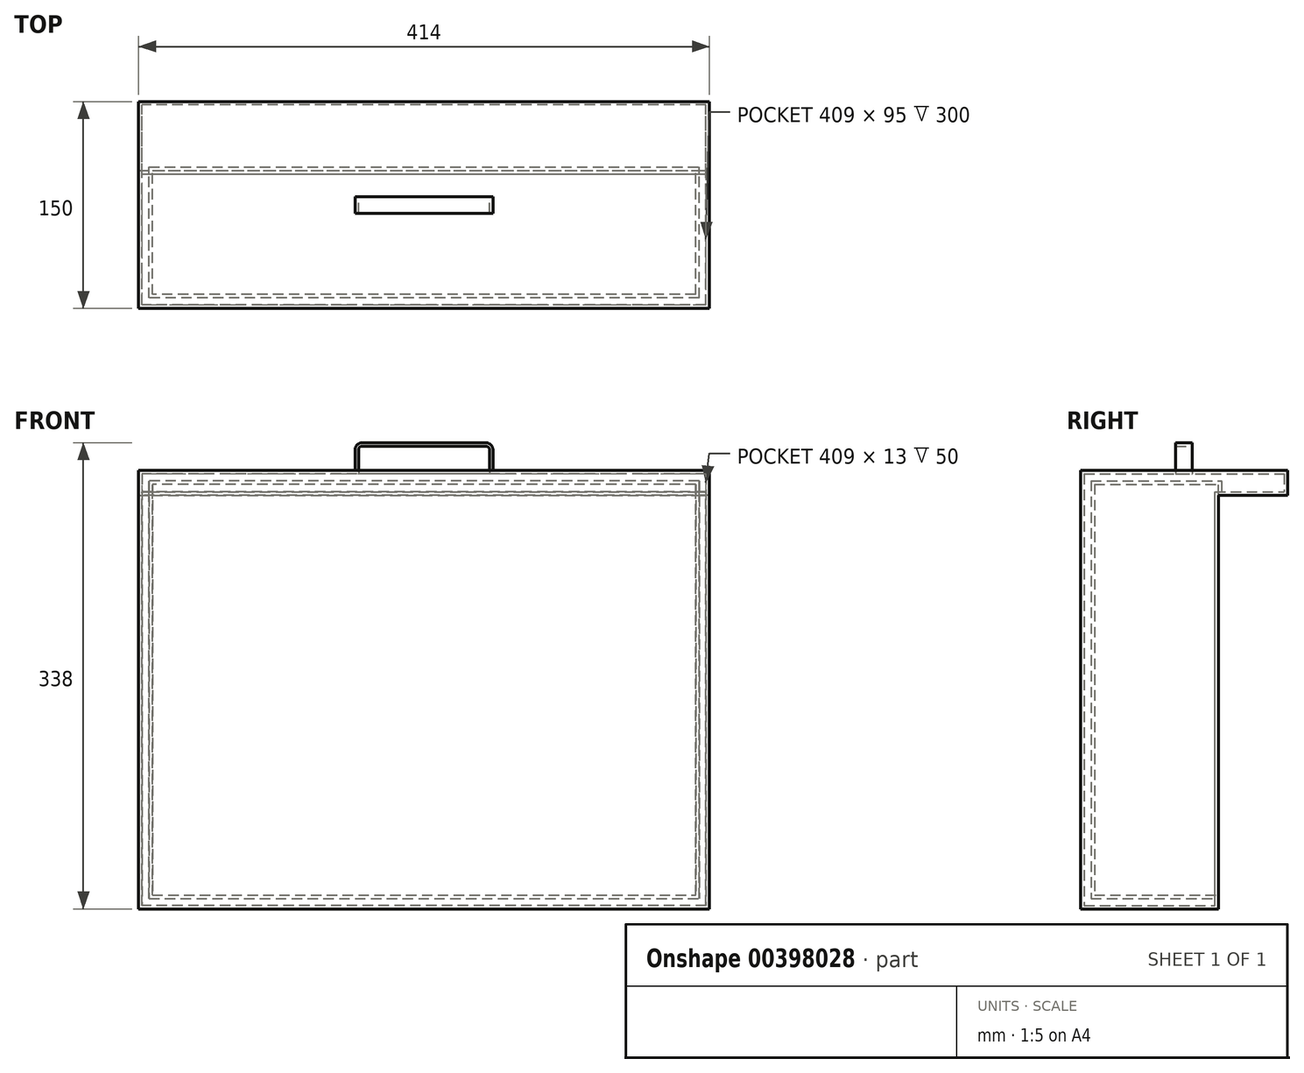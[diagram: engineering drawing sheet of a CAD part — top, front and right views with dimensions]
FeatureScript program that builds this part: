
annotation { "Feature Type Name" : "Feature", "Feature Type Description" : "" }
export const myFeature = defineFeature(function(context is Context, id is Id, definition is map)
    precondition{}
    {
        {
            var Q0;
            Q0=qCreatedBy(makeId("Top.planeOp"),FACE);
            var sketch = newSketch(context, id + "F0", { "sketchPlane" : qUnion([Q0])});
            skLineSegment(sketch, "E0.bottom", {"start": v(207, -75) * mm, "end": v(-207, -75) * mm});
            skLineSegment(sketch, "E0.top", {"start": v(207, 75) * mm, "end": v(-207, 75) * mm});
            skLineSegment(sketch, "E0.left", {"start": v(207, -75) * mm, "end": v(207, 75) * mm});
            skLineSegment(sketch, "E0.right", {"start": v(-207, -75) * mm, "end": v(-207, 75) * mm});
            skPoint(sketch, "E0.middle", {"position": v(0, 0) * mm});
            skSolve(sketch);
        }
        {
            var Q0;
            Q0 = qSketchRegion(id + "F0", true);
            extrude(context, id + "F1", {"entities" : qUnion([Q0]), "depth" : 18 * mm});
        }
        {
            var Q0;
            Q0=makeQuery(id+"F1.opExtrude","CAP_FACE",FACE,{"disambiguationData":[OSD([sQuery(id+"F0.wireOp",EDGE,"E0.bottom"),sQuery(id+"F0.wireOp",EDGE,"E0.top"),sQuery(id+"F0.wireOp",EDGE,"E0.left"),sQuery(id+"F0.wireOp",EDGE,"E0.right")])],"isStart":true});
            var sketch = newSketch(context, id + "F2", { "sketchPlane" : qUnion([Q0])});
            skLineSegment(sketch, "E1.bottom", {"start": v(-207, 75) * mm, "end": v(207, 75) * mm});
            skLineSegment(sketch, "E1.top", {"start": v(-207, -25) * mm, "end": v(207, -25) * mm});
            skLineSegment(sketch, "E1.left", {"start": v(-207, 75) * mm, "end": v(-207, -25) * mm});
            skLineSegment(sketch, "E1.right", {"start": v(207, 75) * mm, "end": v(207, -25) * mm});
            skSolve(sketch);
        }
        {
            var Q0;
            Q0 = qSketchRegion(id + "F2", true);
            extrude(context, id + "F3", {"entities" : qUnion([Q0]), "operationType" : NewBodyOperationType.ADD, "depth" : 300 * mm});
        }
        {
            var Q0;
            Q0=makeQuery(id+"F3.opExtrude","SWEPT_FACE",FACE,{"disambiguationData":[OSD([sQuery(id+"F2.wireOp",EDGE,"E1.top")])]});
            shell(context, id + "F4", {"entities" : qUnion([Q0]), "thickness" : 10 * mm});
        }
        {
            var Q0;
            Q0=makeQuery(id+"F1.opExtrude","CAP_FACE",FACE,{"disambiguationData":[OSD([sQuery(id+"F0.wireOp",EDGE,"E0.bottom"),sQuery(id+"F0.wireOp",EDGE,"E0.top"),sQuery(id+"F0.wireOp",EDGE,"E0.left"),sQuery(id+"F0.wireOp",EDGE,"E0.right")])],"isStart":false});
            var sketch = newSketch(context, id + "F5", { "sketchPlane" : qUnion([Q0])});
            skLineSegment(sketch, "E2.bottom", {"start": v(50, -6) * mm, "end": v(-50, -6) * mm});
            skLineSegment(sketch, "E2.top", {"start": v(50, 6) * mm, "end": v(-50, 6) * mm});
            skLineSegment(sketch, "E2.left", {"start": v(50, -6) * mm, "end": v(50, 6) * mm});
            skLineSegment(sketch, "E2.right", {"start": v(-50, -6) * mm, "end": v(-50, 6) * mm});
            skPoint(sketch, "E2.middle", {"position": v(0, 0) * mm});
            skSolve(sketch);
        }
        {
            var Q0;
            Q0=makeQuery(id+"F5.imprint","IMPRINT",FACE,{"disambiguationData":[TD([[makeQuery(id+"F5.imprint","IMPRINT",EDGE,{"derivedFrom":sQuery(id+"F5.wireOp",EDGE,"E2.bottom")}),-1.0]])]});
            extrude(context, id + "F6", {"entities" : qUnion([Q0]), "operationType" : NewBodyOperationType.ADD, "depth" : 20 * mm});
        }
        {
            var Q0;
            Q0=makeQuery(id+"F6.opExtrude","CAP_EDGE",EDGE,{"disambiguationData":[OSD([sQuery(id+"F5.wireOp",EDGE,"E2.left")])],"isStart":false});
            var Q1;
            Q1=makeQuery(id+"F6.opExtrude","CAP_EDGE",EDGE,{"disambiguationData":[OSD([sQuery(id+"F5.wireOp",EDGE,"E2.right")])],"isStart":false});
            fillet(context, id + "F7", {"entities" : qUnion([Q0, Q1]), "radius" : 5 * mm, "tangentPropagation" : true, "allowEdgeOverflow" : false});
        }
        {
            var Q0;
            Q0=makeQuery(id+"F6.opExtrude","SWEPT_FACE",FACE,{"disambiguationData":[OSD([sQuery(id+"F5.wireOp",EDGE,"E2.bottom")])]});
            var Q1;
            Q1=makeQuery(id+"F6.opExtrude","SWEPT_FACE",FACE,{"disambiguationData":[OSD([sQuery(id+"F5.wireOp",EDGE,"E2.top")])]});
            var Q2;
            Q2=makeQuery(id+"F1.opExtrude","SWEPT_BODY",BODY,{"disambiguationData":[OSD([sQuery(id+"F0.wireOp",EDGE,"E0.bottom"),sQuery(id+"F0.wireOp",EDGE,"E0.top"),sQuery(id+"F0.wireOp",EDGE,"E0.left"),sQuery(id+"F0.wireOp",EDGE,"E0.right")])]});
            shell(context, id + "F8", {"entities" : qUnion([Q0, Q1]), "parts" : qUnion([Q2]), "thickness" : 2.5 * mm});
        }
    });
